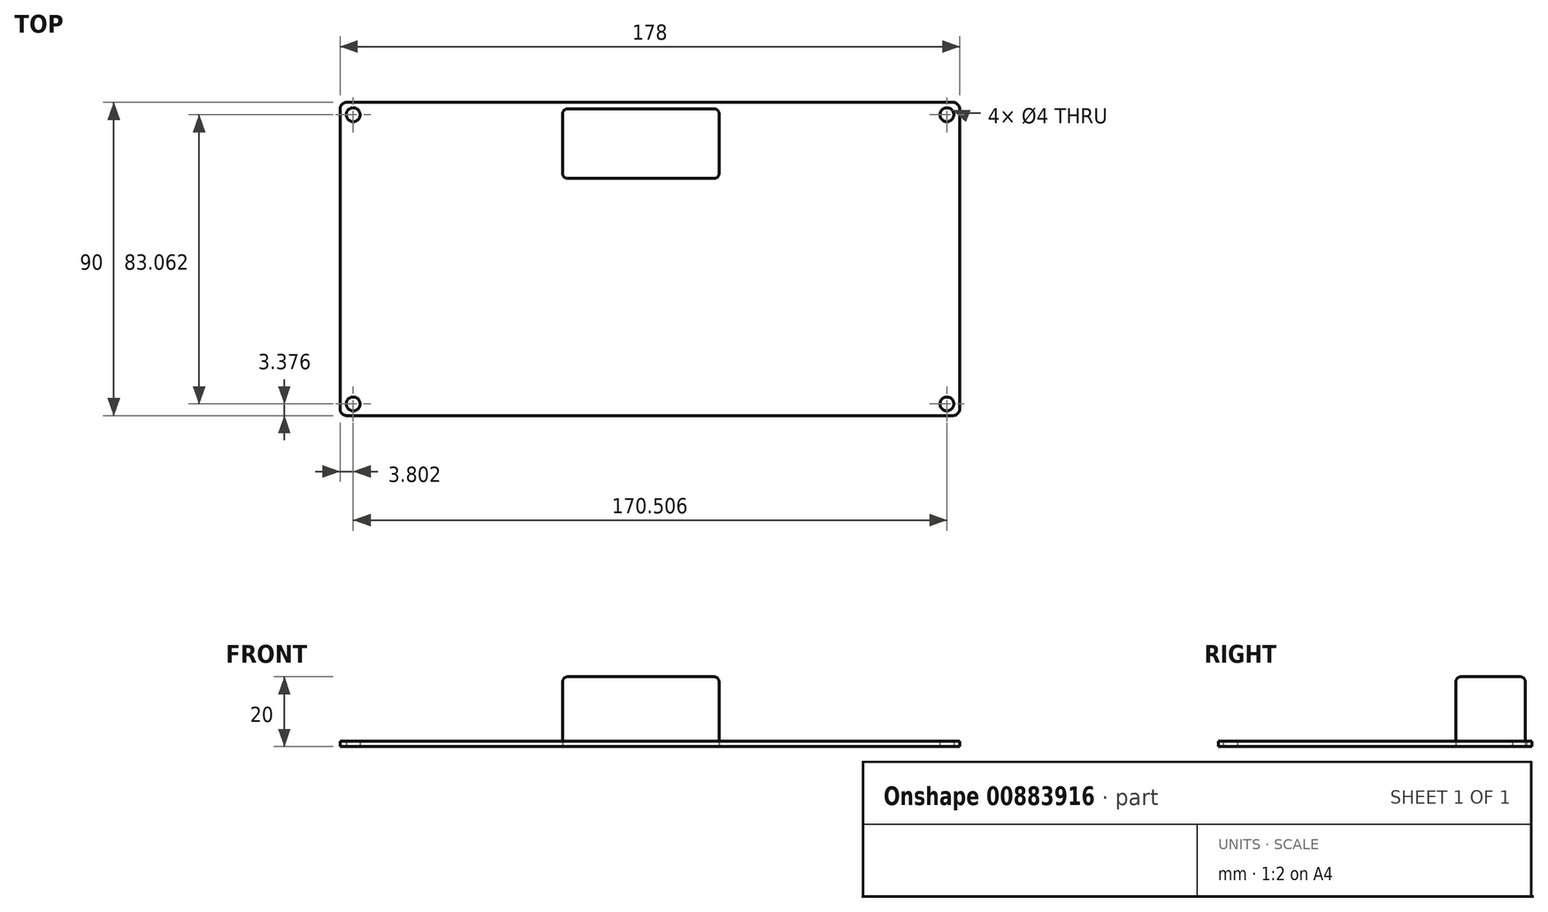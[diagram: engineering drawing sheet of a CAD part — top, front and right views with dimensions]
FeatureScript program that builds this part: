
annotation { "Feature Type Name" : "Feature", "Feature Type Description" : "" }
export const myFeature = defineFeature(function(context is Context, id is Id, definition is map)
    precondition{}
    {
        {
            var Q0;
            Q0=qCreatedBy(makeId("Top.planeOp"),FACE);
            var sketch = newSketch(context, id + "F0", { "sketchPlane" : qUnion([Q0])});
            skLineSegment(sketch, "E0.bottom", {"start": v(-94.56, 59.55) * mm, "end": v(83.44, 59.55) * mm});
            skLineSegment(sketch, "E0.top", {"start": v(-94.56, -30.45) * mm, "end": v(83.44, -30.45) * mm});
            skLineSegment(sketch, "E0.left", {"start": v(-94.56, 59.55) * mm, "end": v(-94.56, -30.45) * mm});
            skLineSegment(sketch, "E0.right", {"start": v(83.44, 59.55) * mm, "end": v(83.44, -30.45) * mm});
            skPoint(sketch, "E1", {"position": v(-90.76, 55.99) * mm});
            skPoint(sketch, "E2", {"position": v(-90.76, -27.07) * mm});
            skPoint(sketch, "E3", {"position": v(79.75, -27.07) * mm});
            skPoint(sketch, "E4", {"position": v(79.75, 55.99) * mm});
            skSolve(sketch);
        }
        {
            var Q0;
            Q0=makeQuery(id+"F0.imprint","IMPRINT",FACE,{"disambiguationData":[TD([[makeQuery(id+"F0.imprint","IMPRINT",EDGE,{"derivedFrom":sQuery(id+"F0.wireOp",EDGE,"E0.bottom")}),-1.0]])]});
            extrude(context, id + "F1", {"entities" : qUnion([Q0]), "depth" : 1.5 * mm, "offsetDistance" : 25 * mm});
        }
        {
            var Q0;
            Q0=makeQuery(id+"F1.opExtrude","SWEPT_EDGE",EDGE,{"disambiguationData":[OSD([sQuery(id+"F0.wireOp",EDGE,"E0.bottom"),sQuery(id+"F0.wireOp",EDGE,"E0.right")])]});
            var Q1;
            Q1=makeQuery(id+"F1.opExtrude","SWEPT_EDGE",EDGE,{"disambiguationData":[OSD([sQuery(id+"F0.wireOp",EDGE,"E0.top"),sQuery(id+"F0.wireOp",EDGE,"E0.right")])]});
            var Q2;
            Q2=makeQuery(id+"F1.opExtrude","SWEPT_EDGE",EDGE,{"disambiguationData":[OSD([sQuery(id+"F0.wireOp",EDGE,"E0.top"),sQuery(id+"F0.wireOp",EDGE,"E0.left")])]});
            var Q3;
            Q3=makeQuery(id+"F1.opExtrude","SWEPT_EDGE",EDGE,{"disambiguationData":[OSD([sQuery(id+"F0.wireOp",EDGE,"E0.bottom"),sQuery(id+"F0.wireOp",EDGE,"E0.left")])]});
            fillet(context, id + "F2", {"entities" : qUnion([Q0, Q1, Q2, Q3]), "radius" : 2 * mm, "tangentPropagation" : true, "allowEdgeOverflow" : false});
        }
        {
            var Q0;
            Q0=qCreatedBy(makeId("Top.planeOp"),FACE);
            var sketch = newSketch(context, id + "F3", { "sketchPlane" : qUnion([Q0])});
            skLineSegment(sketch, "E5.bottom", {"start": v(-30.66, 57.69) * mm, "end": v(14.34, 57.69) * mm});
            skLineSegment(sketch, "E5.top", {"start": v(-30.66, 37.69) * mm, "end": v(14.34, 37.69) * mm});
            skLineSegment(sketch, "E5.left", {"start": v(-30.66, 57.69) * mm, "end": v(-30.66, 37.69) * mm});
            skLineSegment(sketch, "E5.right", {"start": v(14.34, 57.69) * mm, "end": v(14.34, 37.69) * mm});
            skSolve(sketch);
        }
        {
            var Q0;
            Q0=sQuery(id+"F0.wireOp",VERTEX,"E1");
            var Q1;
            Q1=sQuery(id+"F0.wireOp",VERTEX,"E2");
            var Q2;
            Q2=sQuery(id+"F0.wireOp",VERTEX,"E3");
            var Q3;
            Q3=sQuery(id+"F0.wireOp",VERTEX,"E4");
            var Q4;
            Q4=makeQuery(id+"F1.opExtrude","SWEPT_BODY",BODY,{"disambiguationData":[OSD([sQuery(id+"F0.wireOp",EDGE,"E0.bottom"),sQuery(id+"F0.wireOp",EDGE,"E0.top"),sQuery(id+"F0.wireOp",EDGE,"E0.left"),sQuery(id+"F0.wireOp",EDGE,"E0.right")])]});
            hole(context, id + "F4", {"style" : HoleStyle.SIMPLE, "endStyle" : HoleEndStyle.BLIND, "oppositeDirection" : true, "holeDiameter" : 4 * mm, "majorDiameter" : 5 * mm, "holeDepth" : 1.8 * mm, "isTappedThrough" : true, "tappedDepth" : 12 * mm, "tapClearance" : 3, "locations" : qUnion([Q0, Q1, Q2, Q3]), "scope" : qUnion([Q4])});
        }
        {
            var Q0;
            Q0 = qSketchRegion(id + "F3", true);
            extrude(context, id + "F5", {"entities" : qUnion([Q0]), "depth" : 20 * mm, "offsetDistance" : 25 * mm});
        }
        {
            var Q0;
            Q0=makeQuery(id+"F5.opExtrude","CAP_EDGE",EDGE,{"disambiguationData":[OSD([sQuery(id+"F3.wireOp",EDGE,"E5.top")])],"isStart":false});
            var Q1;
            Q1=makeQuery(id+"F5.opExtrude","SWEPT_EDGE",EDGE,{"disambiguationData":[OSD([sQuery(id+"F3.wireOp",EDGE,"E5.top"),sQuery(id+"F3.wireOp",EDGE,"E5.right")])]});
            var Q2;
            Q2=makeQuery(id+"F5.opExtrude","CAP_EDGE",EDGE,{"disambiguationData":[OSD([sQuery(id+"F3.wireOp",EDGE,"E5.right")])],"isStart":false});
            var Q3;
            Q3=makeQuery(id+"F5.opExtrude","SWEPT_EDGE",EDGE,{"disambiguationData":[OSD([sQuery(id+"F3.wireOp",EDGE,"E5.bottom"),sQuery(id+"F3.wireOp",EDGE,"E5.right")])]});
            var Q4;
            Q4=makeQuery(id+"F5.opExtrude","CAP_EDGE",EDGE,{"disambiguationData":[OSD([sQuery(id+"F3.wireOp",EDGE,"E5.bottom")])],"isStart":false});
            var Q5;
            Q5=makeQuery(id+"F5.opExtrude","SWEPT_EDGE",EDGE,{"disambiguationData":[OSD([sQuery(id+"F3.wireOp",EDGE,"E5.bottom"),sQuery(id+"F3.wireOp",EDGE,"E5.left")])]});
            var Q6;
            Q6=makeQuery(id+"F5.opExtrude","CAP_EDGE",EDGE,{"disambiguationData":[OSD([sQuery(id+"F3.wireOp",EDGE,"E5.left")])],"isStart":false});
            var Q7;
            Q7=makeQuery(id+"F5.opExtrude","SWEPT_EDGE",EDGE,{"disambiguationData":[OSD([sQuery(id+"F3.wireOp",EDGE,"E5.top"),sQuery(id+"F3.wireOp",EDGE,"E5.left")])]});
            fillet(context, id + "F6", {"entities" : qUnion([Q0, Q1, Q2, Q3, Q4, Q5, Q6, Q7]), "radius" : 1.5 * mm, "tangentPropagation" : true, "allowEdgeOverflow" : false});
        }
    });
